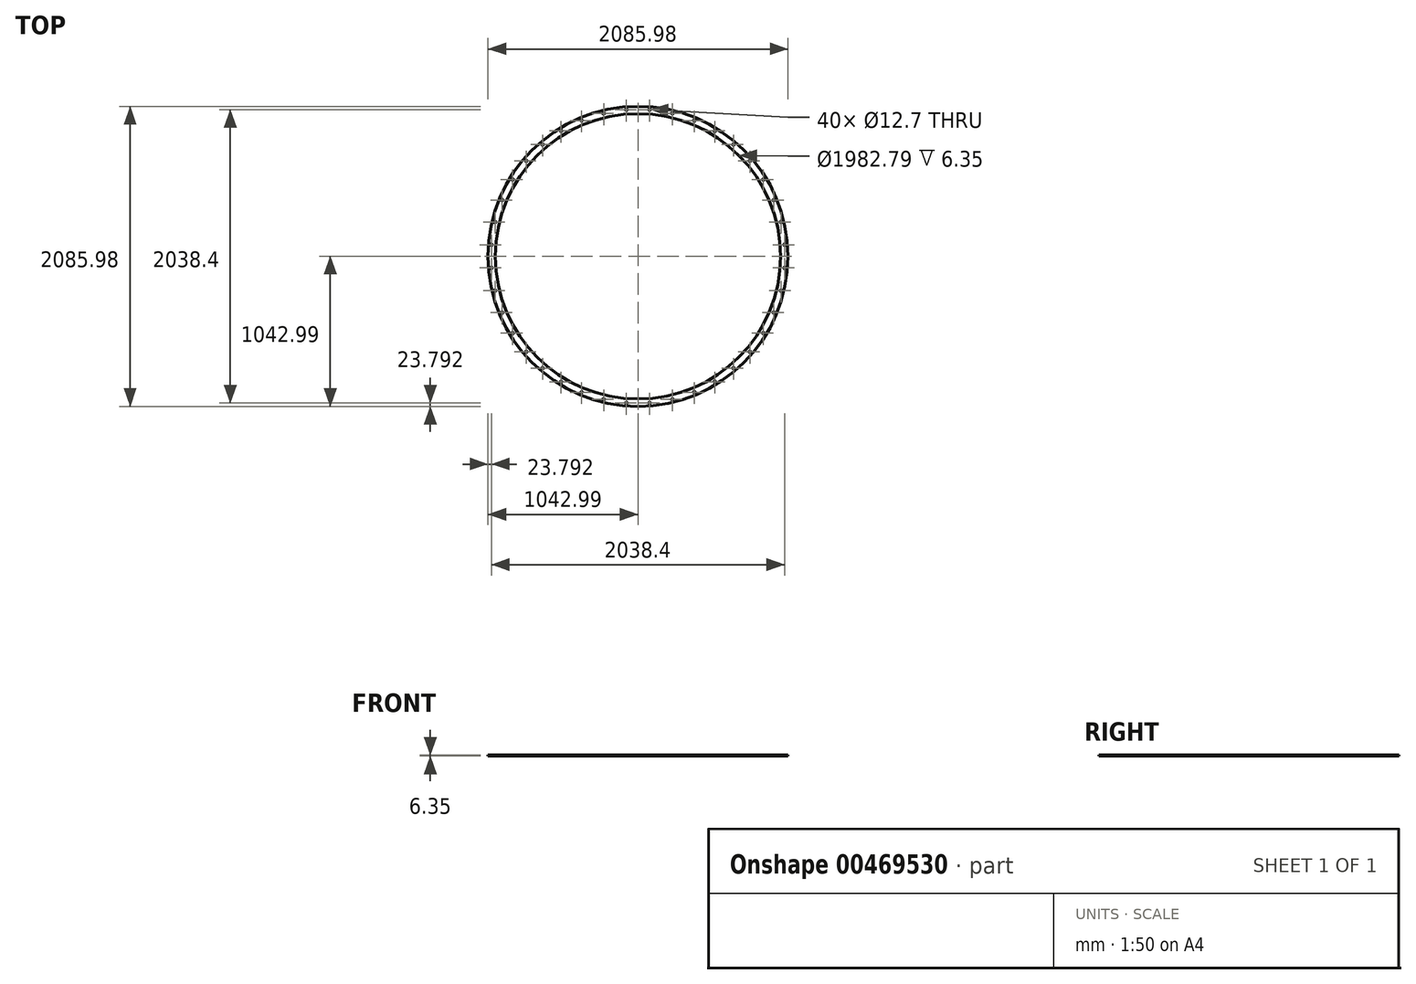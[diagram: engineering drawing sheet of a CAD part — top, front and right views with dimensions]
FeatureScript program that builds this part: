
annotation { "Feature Type Name" : "Feature", "Feature Type Description" : "" }
export const myFeature = defineFeature(function(context is Context, id is Id, definition is map)
    precondition{}
    {
        {
            var Q0;
            Q0=qCreatedBy(makeId("Top.planeOp"),FACE);
            var sketch = newSketch(context, id + "F0", { "sketchPlane" : qUnion([Q0])});
            skCircle(sketch, "E0", {"center": v(0, 0) * mm, "radius": 1042.99 * mm});
            skCircle(sketch, "E1", {"center": v(0, 0) * mm, "radius": 991.4 * mm});
            skCircle(sketch, "E2", {"center": v(0, 0) * mm, "radius": 1022.35 * mm, "construction": true});
            skCircle(sketch, "E3", {"center": v(1019.2, 80.21) * mm, "radius": 6.35 * mm});
            skLineSegment(sketch, "E4", {"start": v(0, 0) * mm, "end": v(1019.2, 80.21) * mm});
            skCircle(sketch, "E5.1.0", {"center": v(994.1, 238.66) * mm, "radius": 6.35 * mm});
            skCircle(sketch, "E5.2.0", {"center": v(944.53, 391.24) * mm, "radius": 6.35 * mm});
            skCircle(sketch, "E5.3.0", {"center": v(871.7, 534.18) * mm, "radius": 6.35 * mm});
            skCircle(sketch, "E5.4.0", {"center": v(777.4, 663.96) * mm, "radius": 6.35 * mm});
            skCircle(sketch, "E5.5.0", {"center": v(663.96, 777.4) * mm, "radius": 6.35 * mm});
            skCircle(sketch, "E5.6.0", {"center": v(534.18, 871.7) * mm, "radius": 6.35 * mm});
            skCircle(sketch, "E5.7.0", {"center": v(391.24, 944.53) * mm, "radius": 6.35 * mm});
            skCircle(sketch, "E5.8.0", {"center": v(238.66, 994.1) * mm, "radius": 6.35 * mm});
            skCircle(sketch, "E5.9.0", {"center": v(80.21, 1019.2) * mm, "radius": 6.35 * mm});
            skCircle(sketch, "E5.10.0", {"center": v(-80.21, 1019.2) * mm, "radius": 6.35 * mm});
            skCircle(sketch, "E5.11.0", {"center": v(-238.66, 994.1) * mm, "radius": 6.35 * mm});
            skCircle(sketch, "E5.12.0", {"center": v(-391.24, 944.53) * mm, "radius": 6.35 * mm});
            skCircle(sketch, "E5.13.0", {"center": v(-534.18, 871.7) * mm, "radius": 6.35 * mm});
            skCircle(sketch, "E5.14.0", {"center": v(-663.96, 777.4) * mm, "radius": 6.35 * mm});
            skCircle(sketch, "E5.15.0", {"center": v(-777.4, 663.96) * mm, "radius": 6.35 * mm});
            skCircle(sketch, "E5.16.0", {"center": v(-871.7, 534.18) * mm, "radius": 6.35 * mm});
            skCircle(sketch, "E5.17.0", {"center": v(-944.53, 391.24) * mm, "radius": 6.35 * mm});
            skCircle(sketch, "E5.18.0", {"center": v(-994.1, 238.66) * mm, "radius": 6.35 * mm});
            skCircle(sketch, "E5.19.0", {"center": v(-1019.2, 80.21) * mm, "radius": 6.35 * mm});
            skCircle(sketch, "E5.20.0", {"center": v(-1019.2, -80.21) * mm, "radius": 6.35 * mm});
            skCircle(sketch, "E5.21.0", {"center": v(-994.1, -238.66) * mm, "radius": 6.35 * mm});
            skCircle(sketch, "E5.22.0", {"center": v(-944.53, -391.24) * mm, "radius": 6.35 * mm});
            skCircle(sketch, "E5.23.0", {"center": v(-871.7, -534.18) * mm, "radius": 6.35 * mm});
            skCircle(sketch, "E5.24.0", {"center": v(-777.4, -663.96) * mm, "radius": 6.35 * mm});
            skCircle(sketch, "E5.25.0", {"center": v(-663.96, -777.4) * mm, "radius": 6.35 * mm});
            skCircle(sketch, "E5.26.0", {"center": v(-534.18, -871.7) * mm, "radius": 6.35 * mm});
            skCircle(sketch, "E5.27.0", {"center": v(-391.24, -944.53) * mm, "radius": 6.35 * mm});
            skCircle(sketch, "E5.28.0", {"center": v(-238.66, -994.1) * mm, "radius": 6.35 * mm});
            skCircle(sketch, "E5.29.0", {"center": v(-80.21, -1019.2) * mm, "radius": 6.35 * mm});
            skCircle(sketch, "E5.30.0", {"center": v(80.21, -1019.2) * mm, "radius": 6.35 * mm});
            skCircle(sketch, "E5.31.0", {"center": v(238.66, -994.1) * mm, "radius": 6.35 * mm});
            skCircle(sketch, "E5.32.0", {"center": v(391.24, -944.53) * mm, "radius": 6.35 * mm});
            skCircle(sketch, "E5.33.0", {"center": v(534.18, -871.7) * mm, "radius": 6.35 * mm});
            skCircle(sketch, "E5.34.0", {"center": v(663.96, -777.4) * mm, "radius": 6.35 * mm});
            skCircle(sketch, "E5.35.0", {"center": v(777.4, -663.96) * mm, "radius": 6.35 * mm});
            skCircle(sketch, "E5.36.0", {"center": v(871.7, -534.18) * mm, "radius": 6.35 * mm});
            skCircle(sketch, "E5.37.0", {"center": v(944.53, -391.24) * mm, "radius": 6.35 * mm});
            skCircle(sketch, "E5.38.0", {"center": v(994.1, -238.66) * mm, "radius": 6.35 * mm});
            skCircle(sketch, "E5.39.0", {"center": v(1019.2, -80.21) * mm, "radius": 6.35 * mm});
            skLineSegment(sketch, "E6", {"start": v(0, 0) * mm, "end": v(1019.2, -80.21) * mm});
            skSolve(sketch);
        }
        {
            var Q0;
            Q0 = qSketchRegion(id + "F0", true);
            extrude(context, id + "F1", {"entities" : qUnion([Q0]), "depth" : 6.35 * mm, "offsetDistance" : 25.4 * mm});
        }
    });
